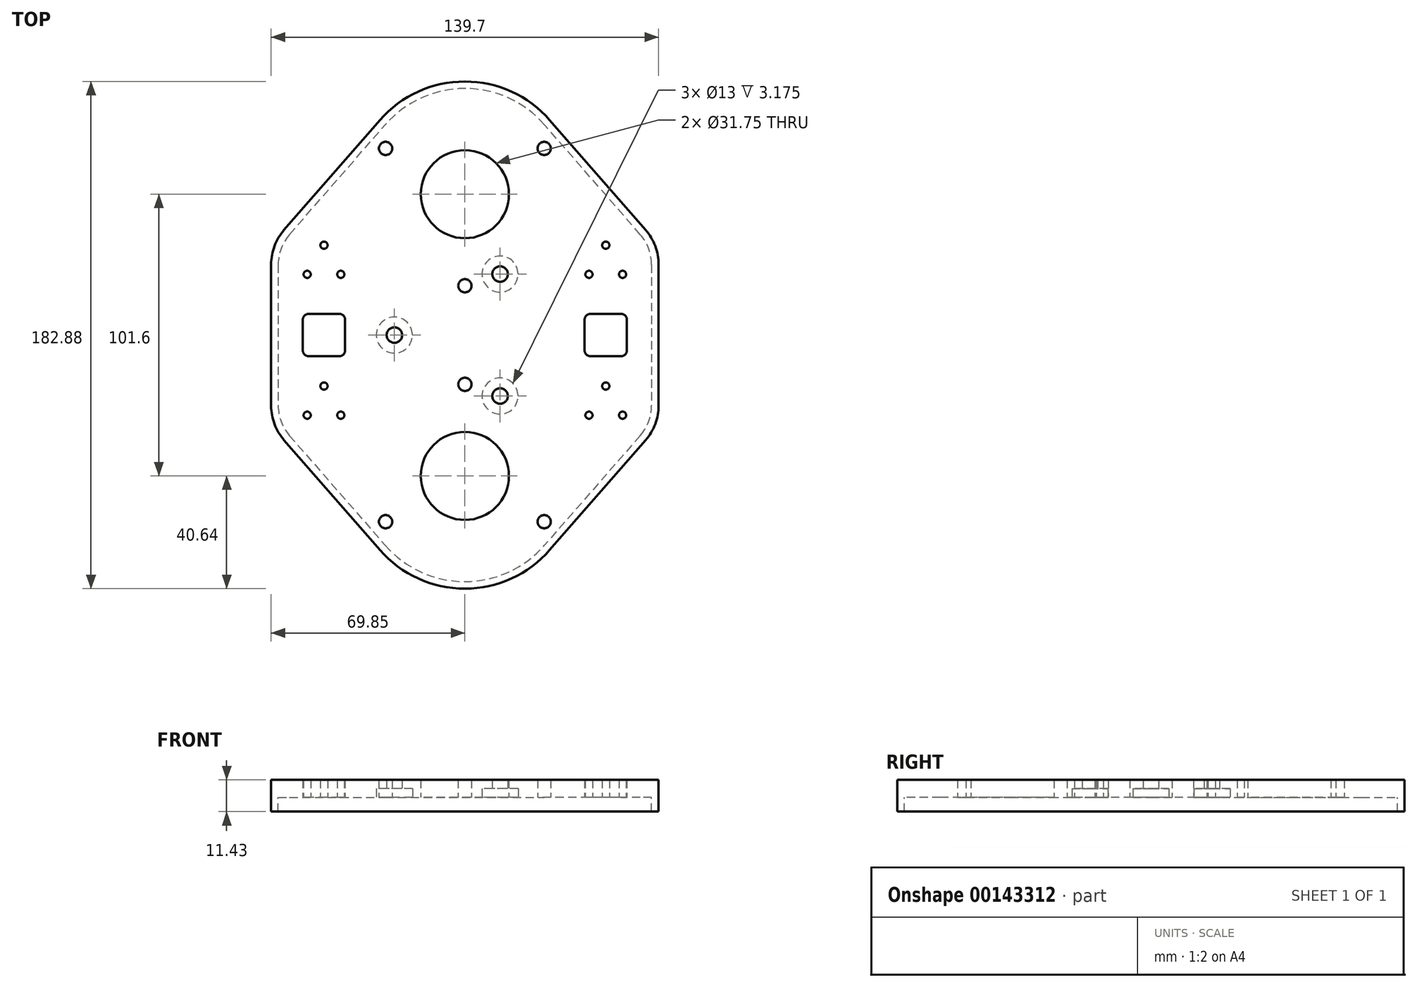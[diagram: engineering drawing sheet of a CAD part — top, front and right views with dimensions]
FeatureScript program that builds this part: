
annotation { "Feature Type Name" : "Feature", "Feature Type Description" : "" }
export const myFeature = defineFeature(function(context is Context, id is Id, definition is map)
    precondition{}
    {
        {
            var Q0;
            Q0=qCreatedBy(makeId("Top.planeOp"),FACE);
            var sketch = newSketch(context, id + "F0", { "sketchPlane" : qUnion([Q0])});
            skLineSegment(sketch, "E0", {"start": v(0, 0) * mm, "end": v(0, 50.8) * mm, "construction": true});
            skLineSegment(sketch, "E1", {"start": v(0, 0) * mm, "end": v(0, -50.8) * mm, "construction": true});
            skCircle(sketch, "E2", {"center": v(0, 50.8) * mm, "radius": 33.02 * mm, "construction": true});
            skLineSegment(sketch, "E3", {"start": v(0, 50.8) * mm, "end": v(0, 83.82) * mm, "construction": true});
            skCircle(sketch, "E4", {"center": v(0, -50.8) * mm, "radius": 33.02 * mm, "construction": true});
            skLineSegment(sketch, "E5", {"start": v(0, -50.8) * mm, "end": v(0, -83.82) * mm, "construction": true});
            skCircle(sketch, "E6", {"center": v(0, 0) * mm, "radius": 25.4 * mm, "construction": true});
            skPoint(sketch, "E7", {"position": v(0, 17.78) * mm});
            skPoint(sketch, "E8", {"position": v(0, -17.78) * mm});
            skCircle(sketch, "E9", {"center": v(0, 17.78) * mm, "radius": 2.39 * mm});
            skCircle(sketch, "E10", {"center": v(0, -17.78) * mm, "radius": 2.39 * mm});
            skCircle(sketch, "E11.1.0", {"center": v(28.6, 67.3) * mm, "radius": 2.39 * mm});
            skCircle(sketch, "E11.2.0", {"center": v(-28.6, 67.31) * mm, "radius": 2.39 * mm});
            skCircle(sketch, "E12.1.0", {"center": v(-28.6, -67.3) * mm, "radius": 2.39 * mm});
            skCircle(sketch, "E12.2.0", {"center": v(28.6, -67.31) * mm, "radius": 2.39 * mm});
            skCircle(sketch, "E13", {"center": v(-25.4, 0) * mm, "radius": 2.8 * mm});
            skCircle(sketch, "E14.1.0", {"center": v(12.7, -22) * mm, "radius": 2.8 * mm});
            skCircle(sketch, "E14.2.0", {"center": v(12.7, 22) * mm, "radius": 2.8 * mm});
            skSolve(sketch);
        }
        {
            var Q0;
            Q0=qCreatedBy(makeId("Top.planeOp"),FACE);
            var sketch = newSketch(context, id + "F1", { "sketchPlane" : qUnion([Q0])});
            skPoint(sketch, "E15", {"position": v(-50.8, 25.4) * mm});
            skLineSegment(sketch, "E16", {"start": v(-50.8, 25.4) * mm, "end": v(-50.8, 32.4) * mm, "construction": true});
            skCircle(sketch, "E17", {"center": v(-50.8, 32.4) * mm, "radius": 1.3 * mm});
            skCircle(sketch, "E18.1.0", {"center": v(-56.86, 21.9) * mm, "radius": 1.3 * mm});
            skCircle(sketch, "E18.2.0", {"center": v(-44.74, 21.9) * mm, "radius": 1.3 * mm});
            skCircle(sketch, "E19", {"center": v(-50.8, 25.4) * mm, "radius": 7 * mm, "construction": true});
            skPoint(sketch, "E20", {"position": v(-50.8, -25.4) * mm});
            skLineSegment(sketch, "E21", {"start": v(-50.8, -25.4) * mm, "end": v(-50.8, -18.4) * mm, "construction": true});
            skCircle(sketch, "E22", {"center": v(-50.8, -18.4) * mm, "radius": 1.3 * mm});
            skCircle(sketch, "E23.1.0", {"center": v(-56.86, -28.9) * mm, "radius": 1.3 * mm});
            skCircle(sketch, "E23.2.0", {"center": v(-44.74, -28.9) * mm, "radius": 1.3 * mm});
            skCircle(sketch, "E24", {"center": v(-50.8, -25.4) * mm, "radius": 7 * mm, "construction": true});
            skPoint(sketch, "E25", {"position": v(50.8, 25.4) * mm});
            skLineSegment(sketch, "E26", {"start": v(50.8, 25.4) * mm, "end": v(50.8, 32.4) * mm, "construction": true});
            skCircle(sketch, "E27", {"center": v(50.8, 32.4) * mm, "radius": 1.3 * mm});
            skCircle(sketch, "E28.1.0", {"center": v(44.74, 21.9) * mm, "radius": 1.3 * mm});
            skCircle(sketch, "E28.2.0", {"center": v(56.86, 21.9) * mm, "radius": 1.3 * mm});
            skCircle(sketch, "E29", {"center": v(50.8, 25.4) * mm, "radius": 7 * mm, "construction": true});
            skPoint(sketch, "E30", {"position": v(50.8, -25.4) * mm});
            skLineSegment(sketch, "E31", {"start": v(50.8, -25.4) * mm, "end": v(50.8, -18.4) * mm, "construction": true});
            skCircle(sketch, "E32", {"center": v(50.8, -18.4) * mm, "radius": 1.3 * mm});
            skCircle(sketch, "E33.1.0", {"center": v(44.74, -28.9) * mm, "radius": 1.3 * mm});
            skCircle(sketch, "E33.2.0", {"center": v(56.86, -28.9) * mm, "radius": 1.3 * mm});
            skCircle(sketch, "E34", {"center": v(50.8, -25.4) * mm, "radius": 7 * mm, "construction": true});
            skLineSegment(sketch, "E35", {"start": v(-50.8, 25.4) * mm, "end": v(50.8, 25.4) * mm, "construction": true});
            skLineSegment(sketch, "E36", {"start": v(-50.8, 25.4) * mm, "end": v(-50.8, -25.4) * mm, "construction": true});
            skLineSegment(sketch, "E37", {"start": v(50.8, -25.4) * mm, "end": v(-50.8, -25.4) * mm, "construction": true});
            skLineSegment(sketch, "E38", {"start": v(50.8, -25.4) * mm, "end": v(50.8, 25.4) * mm, "construction": true});
            skLineSegment(sketch, "E39", {"start": v(-50.8, 0) * mm, "end": v(50.8, 0) * mm, "construction": true});
            skPoint(sketch, "E39.endSnap0", {"position": v(50.8, 0) * mm});
            skLineSegment(sketch, "E40", {"start": v(0, 25.4) * mm, "end": v(0, -25.4) * mm, "construction": true});
            skPoint(sketch, "E41", {"position": v(0, 0) * mm});
            skSolve(sketch);
        }
        {
            var Q0;
            Q0=qCreatedBy(makeId("Top.planeOp"),FACE);
            var sketch = newSketch(context, id + "F2", { "sketchPlane" : qUnion([Q0])});
            skCircle(sketch, "E42", {"center": v(0, -50.8) * mm, "radius": 40.64 * mm});
            skLineSegment(sketch, "E43", {"start": v(-69.85, 25.4) * mm, "end": v(-69.85, -25.4) * mm});
            skLineSegment(sketch, "E44", {"start": v(69.85, 25.4) * mm, "end": v(69.85, -25.4) * mm});
            skLineSegment(sketch, "E45", {"start": v(69.85, 0) * mm, "end": v(50.8, 0) * mm, "construction": true});
            skLineSegment(sketch, "E46", {"start": v(-65.16, 37.92) * mm, "end": v(-30.63, 77.51) * mm});
            skLineSegment(sketch, "E47", {"start": v(65.16, 37.92) * mm, "end": v(30.63, 77.51) * mm});
            skLineSegment(sketch, "E48", {"start": v(-65.16, -37.92) * mm, "end": v(-30.63, -77.51) * mm});
            skLineSegment(sketch, "E49", {"start": v(65.16, -37.92) * mm, "end": v(30.63, -77.51) * mm});
            skPoint(sketch, "E50.visualSharp", {"position": v(-69.85, 32.54) * mm});
            skArc(sketch, "E50.filletArc", {"start": v(-65.16, 37.92) * mm, "mid": v(-68.64, 32.09) * mm, "end": v(-69.85, 25.4) * mm});
            skPoint(sketch, "E51.visualSharp", {"position": v(69.85, 32.54) * mm});
            skArc(sketch, "E51.filletArc", {"start": v(69.85, 25.4) * mm, "mid": v(68.64, 32.09) * mm, "end": v(65.16, 37.92) * mm});
            skPoint(sketch, "E52.visualSharp", {"position": v(69.85, -32.54) * mm});
            skArc(sketch, "E52.filletArc", {"start": v(65.16, -37.92) * mm, "mid": v(68.64, -32.09) * mm, "end": v(69.85, -25.4) * mm});
            skPoint(sketch, "E53.visualSharp", {"position": v(-69.85, -32.54) * mm});
            skArc(sketch, "E53.filletArc", {"start": v(-69.85, -25.4) * mm, "mid": v(-68.64, -32.09) * mm, "end": v(-65.16, -37.92) * mm});
            skCircle(sketch, "E54", {"center": v(-50.8, 32.4) * mm, "radius": 1.3 * mm});
            skCircle(sketch, "E55", {"center": v(-44.74, 21.9) * mm, "radius": 1.3 * mm});
            skCircle(sketch, "E56", {"center": v(-56.86, 21.9) * mm, "radius": 1.3 * mm});
            skCircle(sketch, "E57", {"center": v(-50.8, -18.4) * mm, "radius": 1.3 * mm});
            skCircle(sketch, "E58", {"center": v(-44.74, -28.9) * mm, "radius": 1.3 * mm});
            skCircle(sketch, "E59", {"center": v(-56.86, -28.9) * mm, "radius": 1.3 * mm});
            skCircle(sketch, "E60", {"center": v(50.8, -18.4) * mm, "radius": 1.3 * mm});
            skCircle(sketch, "E61", {"center": v(56.86, -28.9) * mm, "radius": 1.3 * mm});
            skCircle(sketch, "E62", {"center": v(44.74, -28.9) * mm, "radius": 1.3 * mm});
            skCircle(sketch, "E63", {"center": v(-28.6, 67.31) * mm, "radius": 2.39 * mm});
            skCircle(sketch, "E64", {"center": v(28.6, 67.3) * mm, "radius": 2.39 * mm});
            skCircle(sketch, "E65", {"center": v(0, 17.78) * mm, "radius": 2.39 * mm});
            skCircle(sketch, "E66", {"center": v(0, -17.78) * mm, "radius": 2.39 * mm});
            skCircle(sketch, "E67", {"center": v(-28.6, -67.3) * mm, "radius": 2.39 * mm});
            skCircle(sketch, "E68", {"center": v(28.6, -67.31) * mm, "radius": 2.39 * mm});
            skCircle(sketch, "E69", {"center": v(50.8, 32.4) * mm, "radius": 1.3 * mm});
            skCircle(sketch, "E70", {"center": v(44.74, 21.9) * mm, "radius": 1.3 * mm});
            skCircle(sketch, "E71", {"center": v(56.86, 21.9) * mm, "radius": 1.3 * mm});
            skLineSegment(sketch, "E72", {"start": v(-69.85, 0) * mm, "end": v(-50.8, 0) * mm});
            skCircle(sketch, "E73", {"center": v(0, 50.8) * mm, "radius": 40.64 * mm});
            skCircle(sketch, "E74", {"center": v(-25.4, 0) * mm, "radius": 2.8 * mm});
            skCircle(sketch, "E75", {"center": v(12.7, 22) * mm, "radius": 2.8 * mm});
            skCircle(sketch, "E76", {"center": v(12.7, -22) * mm, "radius": 2.8 * mm});
            skSolve(sketch);
        }
        {
            var Q0;
            Q0 = qSketchRegion(id + "F2", true);
            extrude(context, id + "F3", {"entities" : qUnion([Q0]), "depth" : 6.35 * mm, "offsetDistance" : 25.4 * mm});
        }
        {
            var Q0;
            Q0=qCreatedBy(makeId("Top.planeOp"),FACE);
            var sketch = newSketch(context, id + "F4", { "sketchPlane" : qUnion([Q0])});
            skCircle(sketch, "E77", {"center": v(-25.4, 0) * mm, "radius": 6.5 * mm});
            skCircle(sketch, "E78", {"center": v(12.7, 22) * mm, "radius": 6.5 * mm});
            skCircle(sketch, "E79", {"center": v(12.7, -22) * mm, "radius": 6.5 * mm});
            skSolve(sketch);
        }
        {
            var Q0;
            Q0 = qSketchRegion(id + "F4", true);
            extrude(context, id + "F5", {"entities" : qUnion([Q0]), "operationType" : NewBodyOperationType.REMOVE, "depth" : 3.17 * mm, "offsetDistance" : 25.4 * mm});
        }
        {
            var Q0;
            Q0=qCreatedBy(makeId("Top.planeOp"),FACE);
            var sketch = newSketch(context, id + "F6", { "sketchPlane" : qUnion([Q0])});
            skLineSegment(sketch, "E80.0", {"start": v(-65.16, -37.92) * mm, "end": v(-30.63, -77.51) * mm});
            skArc(sketch, "E80.1", {"start": v(-30.63, -77.51) * mm, "mid": v(0, -91.44) * mm, "end": v(30.63, -77.51) * mm});
            skArc(sketch, "E80.2", {"start": v(65.16, -37.92) * mm, "mid": v(68.64, -32.09) * mm, "end": v(69.85, -25.4) * mm});
            skLineSegment(sketch, "E80.3", {"start": v(65.16, -37.92) * mm, "end": v(30.63, -77.51) * mm});
            skLineSegment(sketch, "E80.4", {"start": v(-69.85, 25.4) * mm, "end": v(-69.85, -25.4) * mm});
            skArc(sketch, "E80.5", {"start": v(-69.85, -25.4) * mm, "mid": v(-68.64, -32.09) * mm, "end": v(-65.16, -37.92) * mm});
            skLineSegment(sketch, "E80.6", {"start": v(-65.16, 37.92) * mm, "end": v(-30.63, 77.51) * mm});
            skArc(sketch, "E80.7", {"start": v(-65.16, 37.92) * mm, "mid": v(-68.64, 32.09) * mm, "end": v(-69.85, 25.4) * mm});
            skArc(sketch, "E80.8", {"start": v(30.63, 77.51) * mm, "mid": v(0, 91.44) * mm, "end": v(-30.63, 77.51) * mm});
            skLineSegment(sketch, "E80.9", {"start": v(65.16, 37.92) * mm, "end": v(30.63, 77.51) * mm});
            skArc(sketch, "E80.10", {"start": v(69.85, 25.4) * mm, "mid": v(68.64, 32.09) * mm, "end": v(65.16, 37.92) * mm});
            skLineSegment(sketch, "E80.11", {"start": v(69.85, 25.4) * mm, "end": v(69.85, -25.4) * mm});
            skLineSegment(sketch, "E81.0", {"start": v(-63.24, -36.25) * mm, "end": v(-28.71, -75.84) * mm});
            skArc(sketch, "E81.1", {"start": v(67.3, 25.4) * mm, "mid": v(66.26, 31.2) * mm, "end": v(63.24, 36.25) * mm});
            skLineSegment(sketch, "E81.2", {"start": v(67.3, 25.4) * mm, "end": v(67.3, -25.4) * mm});
            skArc(sketch, "E81.3", {"start": v(63.24, -36.25) * mm, "mid": v(66.26, -31.2) * mm, "end": v(67.31, -25.4) * mm});
            skLineSegment(sketch, "E81.4", {"start": v(63.24, -36.25) * mm, "end": v(28.71, -75.84) * mm});
            skLineSegment(sketch, "E81.5", {"start": v(63.24, 36.25) * mm, "end": v(28.71, 75.84) * mm});
            skArc(sketch, "E81.6", {"start": v(-28.71, -75.84) * mm, "mid": v(0, -88.9) * mm, "end": v(28.71, -75.84) * mm});
            skArc(sketch, "E81.7", {"start": v(28.71, 75.84) * mm, "mid": v(0, 88.9) * mm, "end": v(-28.71, 75.84) * mm});
            skLineSegment(sketch, "E81.8", {"start": v(-63.24, 36.25) * mm, "end": v(-28.71, 75.84) * mm});
            skArc(sketch, "E81.9", {"start": v(-63.24, 36.25) * mm, "mid": v(-66.26, 31.2) * mm, "end": v(-67.3, 25.4) * mm});
            skLineSegment(sketch, "E81.10", {"start": v(-67.31, 25.4) * mm, "end": v(-67.31, -25.4) * mm});
            skArc(sketch, "E81.11", {"start": v(-67.31, -25.4) * mm, "mid": v(-66.26, -31.2) * mm, "end": v(-63.24, -36.25) * mm});
            skSolve(sketch);
        }
        {
            var Q0;
            Q0 = qSketchRegion(id + "F6", true);
            extrude(context, id + "F7", {"entities" : qUnion([Q0]), "operationType" : NewBodyOperationType.ADD, "oppositeDirection" : true, "depth" : 5.08 * mm, "offsetDistance" : 25.4 * mm});
        }
        {
            var Q0;
            Q0=qCreatedBy(makeId("Top.planeOp"),FACE);
            var sketch = newSketch(context, id + "F8", { "sketchPlane" : qUnion([Q0])});
            skCircle(sketch, "E82", {"center": v(0, -50.8) * mm, "radius": 15.88 * mm});
            skCircle(sketch, "E83", {"center": v(0, 50.8) * mm, "radius": 15.88 * mm});
            skLineSegment(sketch, "E84.bottom", {"start": v(-45.21, 7.62) * mm, "end": v(-56.39, 7.62) * mm});
            skLineSegment(sketch, "E84.top", {"start": v(-45.21, -7.62) * mm, "end": v(-56.39, -7.62) * mm});
            skLineSegment(sketch, "E84.left", {"start": v(-43.18, 5.59) * mm, "end": v(-43.18, -5.59) * mm});
            skLineSegment(sketch, "E84.right", {"start": v(-58.42, 5.59) * mm, "end": v(-58.42, -5.59) * mm});
            skPoint(sketch, "E84.middle", {"position": v(-50.8, 0) * mm});
            skLineSegment(sketch, "E85.bottom", {"start": v(56.39, 7.62) * mm, "end": v(45.21, 7.62) * mm});
            skLineSegment(sketch, "E85.top", {"start": v(56.39, -7.62) * mm, "end": v(45.21, -7.62) * mm});
            skLineSegment(sketch, "E85.left", {"start": v(58.42, 5.59) * mm, "end": v(58.42, -5.59) * mm});
            skLineSegment(sketch, "E85.right", {"start": v(43.18, 5.59) * mm, "end": v(43.18, -5.59) * mm});
            skPoint(sketch, "E85.middle", {"position": v(50.8, 0) * mm});
            skLineSegment(sketch, "E86", {"start": v(-50.8, 0) * mm, "end": v(0, 0) * mm, "construction": true});
            skLineSegment(sketch, "E87", {"start": v(0, 0) * mm, "end": v(50.8, 0) * mm, "construction": true});
            skPoint(sketch, "E88.visualSharp", {"position": v(-43.18, -7.62) * mm});
            skArc(sketch, "E88.filletArc", {"start": v(-45.21, -7.62) * mm, "mid": v(-43.78, -7.02) * mm, "end": v(-43.18, -5.59) * mm});
            skPoint(sketch, "E89.visualSharp", {"position": v(-58.42, -7.62) * mm});
            skArc(sketch, "E89.filletArc", {"start": v(-58.42, -5.59) * mm, "mid": v(-57.82, -7.02) * mm, "end": v(-56.39, -7.62) * mm});
            skPoint(sketch, "E90.visualSharp", {"position": v(-58.42, 7.62) * mm});
            skArc(sketch, "E90.filletArc", {"start": v(-56.39, 7.62) * mm, "mid": v(-57.82, 7.02) * mm, "end": v(-58.42, 5.59) * mm});
            skPoint(sketch, "E91.visualSharp", {"position": v(-43.18, 7.62) * mm});
            skArc(sketch, "E91.filletArc", {"start": v(-43.18, 5.59) * mm, "mid": v(-43.78, 7.02) * mm, "end": v(-45.21, 7.62) * mm});
            skPoint(sketch, "E92.visualSharp", {"position": v(58.42, -7.62) * mm});
            skArc(sketch, "E92.filletArc", {"start": v(56.39, -7.62) * mm, "mid": v(57.82, -7.02) * mm, "end": v(58.42, -5.59) * mm});
            skPoint(sketch, "E93.visualSharp", {"position": v(58.42, 7.62) * mm});
            skArc(sketch, "E93.filletArc", {"start": v(58.42, 5.59) * mm, "mid": v(57.82, 7.02) * mm, "end": v(56.39, 7.62) * mm});
            skPoint(sketch, "E94.visualSharp", {"position": v(43.18, 7.62) * mm});
            skArc(sketch, "E94.filletArc", {"start": v(45.21, 7.62) * mm, "mid": v(43.78, 7.02) * mm, "end": v(43.18, 5.59) * mm});
            skPoint(sketch, "E95.visualSharp", {"position": v(43.18, -7.62) * mm});
            skArc(sketch, "E95.filletArc", {"start": v(43.18, -5.59) * mm, "mid": v(43.78, -7.02) * mm, "end": v(45.21, -7.62) * mm});
            skSolve(sketch);
        }
        {
            var Q0;
            Q0 = qSketchRegion(id + "F8", true);
            extrude(context, id + "F9", {"entities" : qUnion([Q0]), "operationType" : NewBodyOperationType.REMOVE, "depth" : 25.4 * mm, "offsetDistance" : 25.4 * mm});
        }
    });
